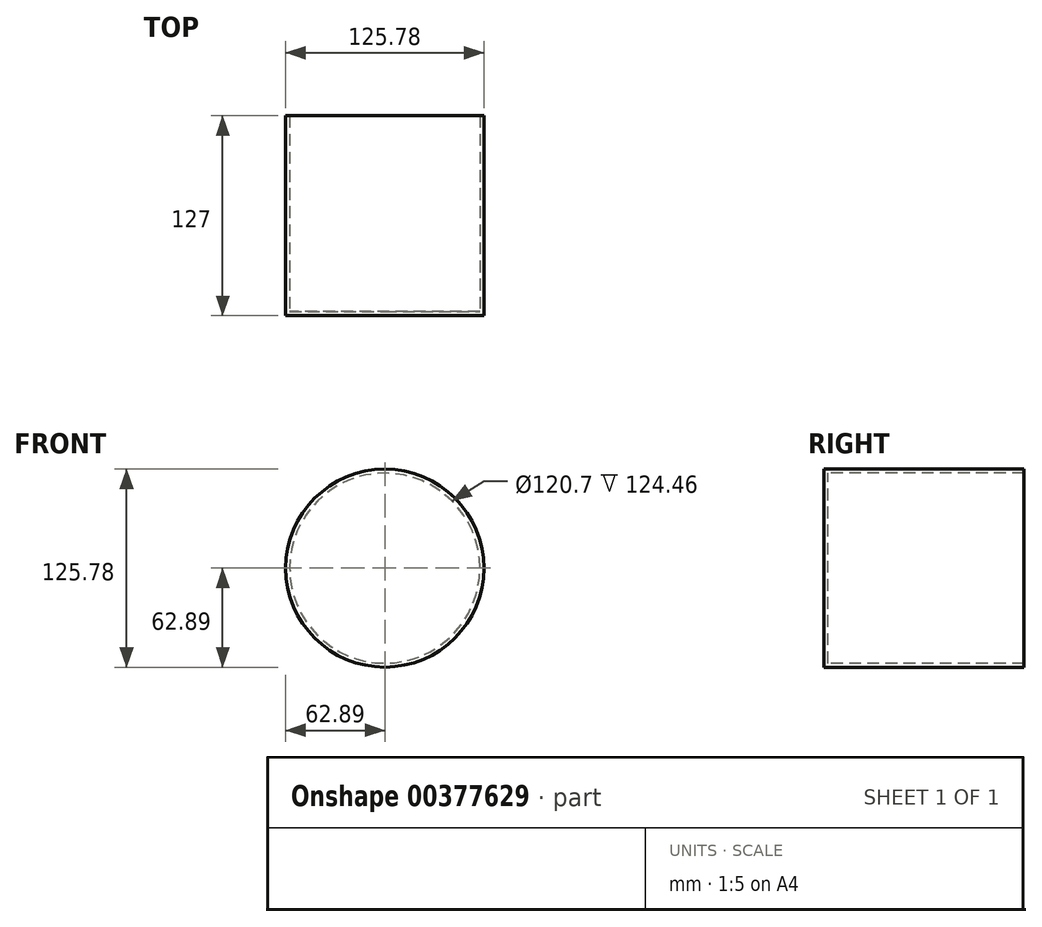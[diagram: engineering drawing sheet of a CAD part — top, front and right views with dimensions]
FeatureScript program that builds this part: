
annotation { "Feature Type Name" : "Feature", "Feature Type Description" : "" }
export const myFeature = defineFeature(function(context is Context, id is Id, definition is map)
    precondition{}
    {
        {
            var Q0;
            Q0=qCreatedBy(makeId("Front.planeOp"),FACE);
            var sketch = newSketch(context, id + "F0", { "sketchPlane" : qUnion([Q0])});
            skCircle(sketch, "E0", {"center": v(0, 0) * mm, "radius": 62.9 * mm});
            skSolve(sketch);
        }
        {
            var Q0;
            Q0=makeQuery(id+"F0.imprint","IMPRINT",FACE,{"disambiguationData":[TD([[makeQuery(id+"F0.imprint","IMPRINT",EDGE,{"derivedFrom":sQuery(id+"F0.wireOp",EDGE,"E0")}),1.0]])]});
            extrude(context, id + "F1", {"entities" : qUnion([Q0]), "oppositeDirection" : true, "depth" : 127 * mm});
        }
        {
            var Q0;
            Q0=makeQuery(id+"F1.opExtrude","CAP_FACE",FACE,{"disambiguationData":[OSD([sQuery(id+"F0.wireOp",EDGE,"E0")])],"isStart":false});
            shell(context, id + "F2", {"entities" : qUnion([Q0]), "thickness" : 2.54 * mm});
        }
    });
